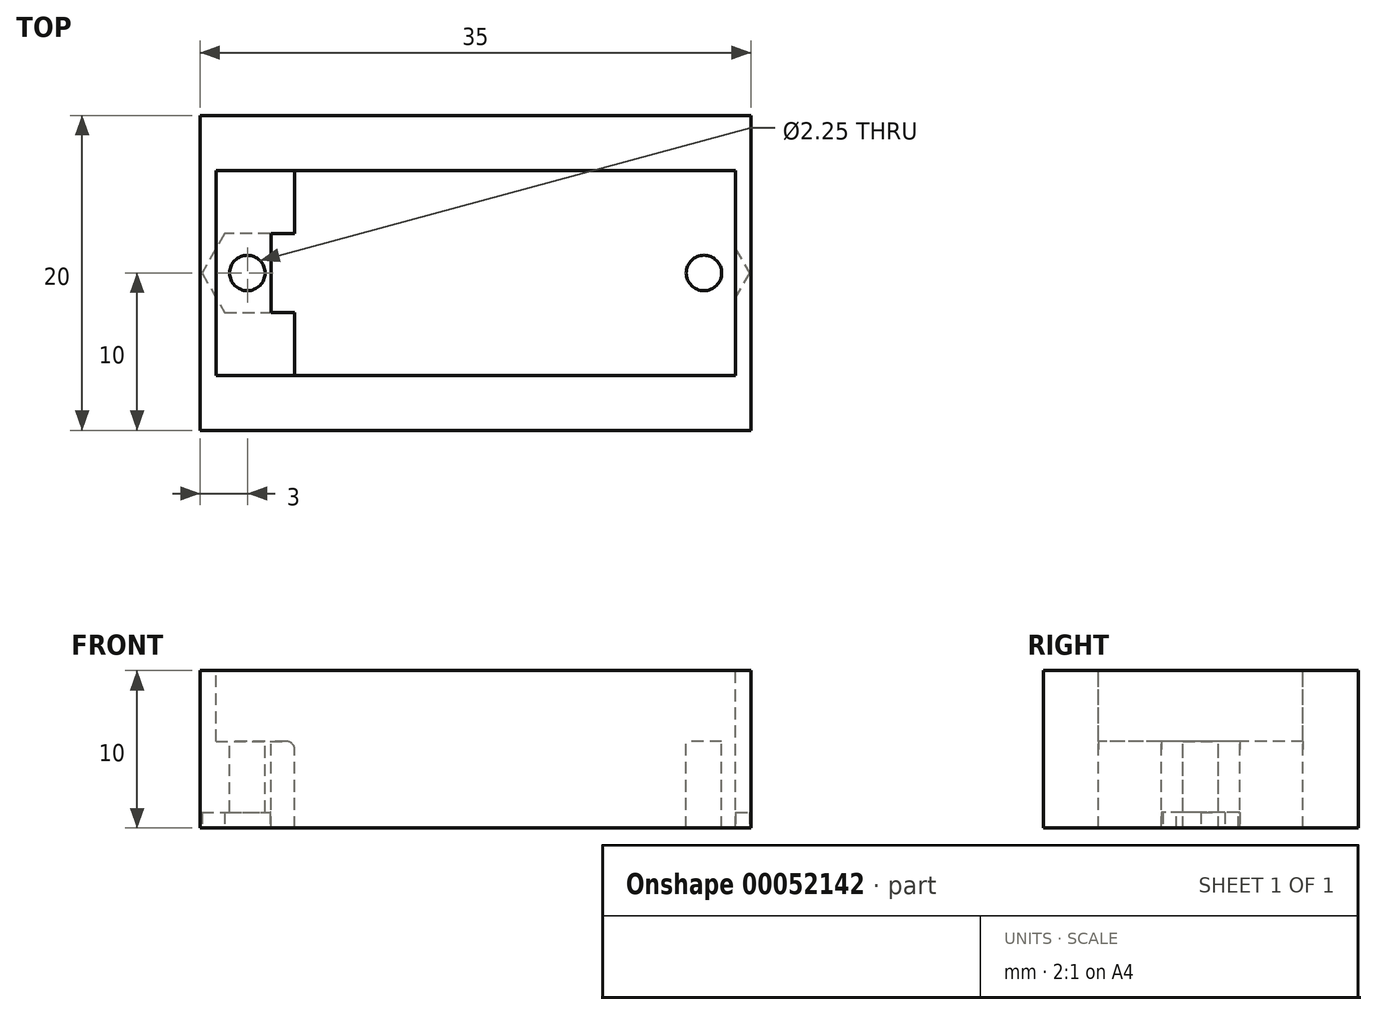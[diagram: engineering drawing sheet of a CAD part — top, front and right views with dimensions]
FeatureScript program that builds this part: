
annotation { "Feature Type Name" : "Feature", "Feature Type Description" : "" }
export const myFeature = defineFeature(function(context is Context, id is Id, definition is map)
    precondition{}
    {
        {
            var Q0;
            Q0=qCreatedBy(makeId("Top.planeOp"),FACE);
            var sketch = newSketch(context, id + "F0", { "sketchPlane" : qUnion([Q0])});
            skLineSegment(sketch, "E0.rect.bottom", {"start": v(-17.5, 10) * mm, "end": v(17.5, 10) * mm});
            skLineSegment(sketch, "E0.rect.top", {"start": v(-17.5, -10) * mm, "end": v(17.5, -10) * mm});
            skLineSegment(sketch, "E0.rect.left", {"start": v(-17.5, 10) * mm, "end": v(-17.5, -10) * mm});
            skLineSegment(sketch, "E0.rect.right", {"start": v(17.5, 10) * mm, "end": v(17.5, -10) * mm});
            skPoint(sketch, "E0.rect.middle", {"position": v(0, 0) * mm});
            skSolve(sketch);
        }
        {
            var Q0;
            Q0=makeQuery(id+"F0.imprint","IMPRINT",FACE,{"disambiguationData":[TD([[makeQuery(id+"F0.imprint","IMPRINT",EDGE,{"derivedFrom":sQuery(id+"F0.wireOp",EDGE,"E0.rect.bottom")}),-1.0]])]});
            extrude(context, id + "F1", {"entities" : qUnion([Q0]), "oppositeDirection" : true, "depth" : 10 * mm});
        }
        {
            var Q0;
            Q0=qCreatedBy(makeId("Top.planeOp"),FACE);
            var sketch = newSketch(context, id + "F2", { "sketchPlane" : qUnion([Q0])});
            skLineSegment(sketch, "E1.rect.bottom", {"start": v(11.5, -6.5) * mm, "end": v(-11.5, -6.5) * mm});
            skLineSegment(sketch, "E1.rect.top", {"start": v(11.5, 6.5) * mm, "end": v(-11.5, 6.5) * mm});
            skLineSegment(sketch, "E1.rect.left", {"start": v(11.5, -6.5) * mm, "end": v(11.5, 6.5) * mm});
            skLineSegment(sketch, "E1.rect.right", {"start": v(-11.5, -6.5) * mm, "end": v(-11.5, 6.5) * mm});
            skPoint(sketch, "E1.rect.middle", {"position": v(0, 0) * mm});
            skSolve(sketch);
        }
        {
            var Q0;
            Q0=makeQuery(id+"F2.imprint","IMPRINT",FACE,{"disambiguationData":[TD([[makeQuery(id+"F2.imprint","IMPRINT",EDGE,{"derivedFrom":sQuery(id+"F2.wireOp",EDGE,"E1.rect.bottom")}),-1.0]])]});
            var Q1;
            Q1=makeQuery(id+"F1.opExtrude","CAP_FACE",FACE,{"disambiguationData":[OSD([sQuery(id+"F0.wireOp",EDGE,"E0.rect.bottom"),sQuery(id+"F0.wireOp",EDGE,"E0.rect.top"),sQuery(id+"F0.wireOp",EDGE,"E0.rect.left"),sQuery(id+"F0.wireOp",EDGE,"E0.rect.right")])],"isStart":false});
            extrude(context, id + "F3", {"entities" : qUnion([Q0]), "operationType" : NewBodyOperationType.REMOVE, "endBound" : BoundingType.UP_TO_SURFACE, "oppositeDirection" : true, "endBoundEntityFace" : qUnion([Q1]), "depth" : 24 * mm});
        }
        {
            var Q0;
            Q0=qCreatedBy(makeId("Top.planeOp"),FACE);
            var sketch = newSketch(context, id + "F4", { "sketchPlane" : qUnion([Q0])});
            skLineSegment(sketch, "E2.rect.bottom", {"start": v(-16.5, 6.5) * mm, "end": v(16.5, 6.5) * mm});
            skLineSegment(sketch, "E2.rect.top", {"start": v(-16.5, -6.5) * mm, "end": v(16.5, -6.5) * mm});
            skLineSegment(sketch, "E2.rect.left", {"start": v(-16.5, 6.5) * mm, "end": v(-16.5, -6.5) * mm});
            skLineSegment(sketch, "E2.rect.right", {"start": v(16.5, 6.5) * mm, "end": v(16.5, -6.5) * mm});
            skPoint(sketch, "E2.rect.middle", {"position": v(0, 0) * mm});
            skSolve(sketch);
        }
        {
            var Q0;
            Q0=makeQuery(id+"F4.imprint","IMPRINT",FACE,{"disambiguationData":[TD([[makeQuery(id+"F4.imprint","IMPRINT",EDGE,{"derivedFrom":sQuery(id+"F4.wireOp",EDGE,"E2.rect.bottom")}),-1.0]])]});
            extrude(context, id + "F5", {"entities" : qUnion([Q0]), "operationType" : NewBodyOperationType.REMOVE, "oppositeDirection" : true, "depth" : 4.5 * mm});
        }
        {
            var Q0;
            Q0=makeQuery(id+"F5.boolean.opBoolean","COPY",FACE,{"disambiguationData":[OD(0.0)],"derivedFrom":makeQuery(id+"F5.opExtrude","CAP_FACE",FACE,{"disambiguationData":[OSD([sQuery(id+"F4.wireOp",EDGE,"E2.rect.bottom"),sQuery(id+"F4.wireOp",EDGE,"E2.rect.top"),sQuery(id+"F4.wireOp",EDGE,"E2.rect.left"),sQuery(id+"F4.wireOp",EDGE,"E2.rect.right")])],"isStart":false})});
            var sketch = newSketch(context, id + "F6", { "sketchPlane" : qUnion([Q0])});
            skCircle(sketch, "E3", {"center": v(-14.5, 0) * mm, "radius": 1.13 * mm});
            skPoint(sketch, "E3.centerSnap0", {"position": v(-11.5, 0) * mm});
            skCircle(sketch, "E4.MirrorC", {"center": v(14.5, 0) * mm, "radius": 1.13 * mm});
            skLineSegment(sketch, "E5.bottom", {"start": v(-11.5, 2.5) * mm, "end": v(-13, 2.5) * mm});
            skLineSegment(sketch, "E5.top", {"start": v(-11.5, -2.5) * mm, "end": v(-13, -2.5) * mm});
            skLineSegment(sketch, "E5.left", {"start": v(-11.5, 2.5) * mm, "end": v(-11.5, -2.5) * mm});
            skLineSegment(sketch, "E5.right", {"start": v(-13, 2.5) * mm, "end": v(-13, -2.5) * mm});
            skLineSegment(sketch, "E6.MirrorCS", {"start": v(11.5, 2.5) * mm, "end": v(13, 2.5) * mm});
            skLineSegment(sketch, "E7.MirrorCS", {"start": v(13, 2.5) * mm, "end": v(13, -2.5) * mm});
            skLineSegment(sketch, "E8.MirrorCS", {"start": v(11.5, -2.5) * mm, "end": v(13, -2.5) * mm});
            skLineSegment(sketch, "E9.MirrorCS", {"start": v(11.5, 2.5) * mm, "end": v(11.5, -2.5) * mm});
            skSolve(sketch);
        }
        {
            var Q0;
            Q0=makeQuery(id+"F6.imprint","IMPRINT",FACE,{"disambiguationData":[TD([[makeQuery(id+"F6.imprint","IMPRINT",EDGE,{"derivedFrom":sQuery(id+"F6.wireOp",EDGE,"E3")}),1.0]])]});
            var Q1;
            Q1=makeQuery(id+"F6.imprint","IMPRINT",FACE,{"disambiguationData":[TD([[makeQuery(id+"F6.imprint","IMPRINT",EDGE,{"derivedFrom":sQuery(id+"F6.wireOp",EDGE,"E4.MirrorC")}),-1.0]])]});
            var Q2;
            Q2=makeQuery(id+"F6.imprint","IMPRINT",FACE,{"disambiguationData":[TD([[makeQuery(id+"F6.imprint","IMPRINT",EDGE,{"derivedFrom":sQuery(id+"F6.wireOp",EDGE,"E5.bottom")}),1.0]])]});
            var Q3;
            Q3=makeQuery(id+"F6.imprint","IMPRINT",FACE,{"disambiguationData":[TD([[makeQuery(id+"F6.imprint","IMPRINT",EDGE,{"derivedFrom":sQuery(id+"F6.wireOp",EDGE,"E6.MirrorCS")}),-1.0]])]});
            var Q4;
            Q4=makeQuery(id+"F1.opExtrude","CAP_FACE",FACE,{"disambiguationData":[OSD([sQuery(id+"F0.wireOp",EDGE,"E0.rect.bottom"),sQuery(id+"F0.wireOp",EDGE,"E0.rect.top"),sQuery(id+"F0.wireOp",EDGE,"E0.rect.left"),sQuery(id+"F0.wireOp",EDGE,"E0.rect.right")])],"isStart":false});
            extrude(context, id + "F7", {"entities" : qUnion([Q0, Q1, Q2, Q3]), "operationType" : NewBodyOperationType.REMOVE, "endBound" : BoundingType.UP_TO_SURFACE, "oppositeDirection" : true, "endBoundEntityFace" : qUnion([Q4]), "depth" : 25 * mm});
        }
        {
            var Q0;
            Q0=makeQuery(id+"F1.opExtrude","CAP_FACE",FACE,{"disambiguationData":[OSD([sQuery(id+"F0.wireOp",EDGE,"E0.rect.bottom"),sQuery(id+"F0.wireOp",EDGE,"E0.rect.top"),sQuery(id+"F0.wireOp",EDGE,"E0.rect.left"),sQuery(id+"F0.wireOp",EDGE,"E0.rect.right")])],"isStart":false});
            var sketch = newSketch(context, id + "F8", { "sketchPlane" : qUnion([Q0])});
            skCircle(sketch, "E10.cCircle", {"center": v(-14.5, 0) * mm, "radius": 2.5 * mm, "construction": true});
            skLineSegment(sketch, "E10.0", {"start": v(-13.06, -2.5) * mm, "end": v(-15.94, -2.5) * mm});
            skLineSegment(sketch, "E10.1", {"start": v(-15.94, -2.5) * mm, "end": v(-17.39, 0) * mm});
            skLineSegment(sketch, "E10.2", {"start": v(-17.39, 0) * mm, "end": v(-15.94, 2.5) * mm});
            skLineSegment(sketch, "E10.3", {"start": v(-15.94, 2.5) * mm, "end": v(-13.06, 2.5) * mm});
            skLineSegment(sketch, "E10.4", {"start": v(-13.06, 2.5) * mm, "end": v(-11.61, 0) * mm});
            skLineSegment(sketch, "E10.5", {"start": v(-11.61, 0) * mm, "end": v(-13.06, -2.5) * mm});
            skPoint(sketch, "E10.0.midPoint", {"position": v(-14.5, -2.5) * mm});
            skCircle(sketch, "E11.MirrorC", {"center": v(14.5, 0) * mm, "radius": 2.5 * mm, "construction": true});
            skLineSegment(sketch, "E12.MirrorCS", {"start": v(15.94, -2.5) * mm, "end": v(17.39, 0) * mm});
            skLineSegment(sketch, "E13.MirrorCS", {"start": v(17.39, 0) * mm, "end": v(15.94, 2.5) * mm});
            skLineSegment(sketch, "E14.MirrorCS", {"start": v(15.94, 2.5) * mm, "end": v(13.06, 2.5) * mm});
            skLineSegment(sketch, "E15.MirrorCS", {"start": v(13.06, 2.5) * mm, "end": v(11.61, 0) * mm});
            skLineSegment(sketch, "E16.MirrorCS", {"start": v(11.61, 0) * mm, "end": v(13.06, -2.5) * mm});
            skLineSegment(sketch, "E17.MirrorCS", {"start": v(13.06, -2.5) * mm, "end": v(15.94, -2.5) * mm});
            skSolve(sketch);
        }
        {
            var Q0;
            {var subQ1=sQuery(id+"F8.wireOp",EDGE,"E10.0");Q0=makeQuery(id+"F8.imprint","IMPRINT",FACE,{"disambiguationData":[TD([[makeQuery(id+"F8.imprint","IMPRINT",EDGE,{"derivedFrom":subQ1}),-1.0]])]});}
            var Q1;
            Q1=makeQuery(id+"F8.imprint","IMPRINT",FACE,{"disambiguationData":[TD([[makeQuery(id+"F8.imprint","IMPRINT",EDGE,{"derivedFrom":sQuery(id+"F8.wireOp",EDGE,"E12.MirrorCS")}),1.0]])]});
            extrude(context, id + "F9", {"entities" : qUnion([Q0, Q1]), "operationType" : NewBodyOperationType.REMOVE, "oppositeDirection" : true, "depth" : 1 * mm});
        }
        {
            var Q0;
            {var subQ0=sQuery(id+"F2.wireOp",EDGE,"E1.rect.right");Q0=makeQuery(id+"F7.boolean.opBoolean","SPLIT",EDGE,{"disambiguationData":[TD([makeQuery(id+"F3.boolean.opBoolean","COPY",FACE,{"derivedFrom":makeQuery(id+"F3.opExtrude","SWEPT_FACE",FACE,{"disambiguationData":[OSD([sQuery(id+"F2.wireOp",EDGE,"E1.rect.top")])]})})])],"derivedFrom":makeQuery(id+"F3.boolean.opBoolean","COPY",EDGE,{"derivedFrom":makeQuery(id+"F3.opExtrude","CAP_EDGE",EDGE,{"disambiguationData":[OSD([subQ0])],"isStart":false})})});}
            var Q1;
            {var subQ0=sQuery(id+"F2.wireOp",EDGE,"E1.rect.right");Q1=makeQuery(id+"F7.boolean.opBoolean","SPLIT",EDGE,{"disambiguationData":[TD([makeQuery(id+"F3.boolean.opBoolean","COPY",FACE,{"derivedFrom":makeQuery(id+"F3.opExtrude","SWEPT_FACE",FACE,{"disambiguationData":[OSD([sQuery(id+"F2.wireOp",EDGE,"E1.rect.bottom")])]})})])],"derivedFrom":makeQuery(id+"F3.boolean.opBoolean","COPY",EDGE,{"derivedFrom":makeQuery(id+"F3.opExtrude","CAP_EDGE",EDGE,{"disambiguationData":[OSD([subQ0])],"isStart":false})})});}
            var Q2;
            Q2=makeQuery(id+"F3.boolean.opBoolean","COPY",EDGE,{"derivedFrom":makeQuery(id+"F3.opExtrude","CAP_EDGE",EDGE,{"disambiguationData":[OSD([sQuery(id+"F2.wireOp",EDGE,"E1.rect.bottom")])],"isStart":false})});
            var Q3;
            Q3=makeQuery(id+"F3.boolean.opBoolean","COPY",EDGE,{"derivedFrom":makeQuery(id+"F3.opExtrude","CAP_EDGE",EDGE,{"disambiguationData":[OSD([sQuery(id+"F2.wireOp",EDGE,"E1.rect.top")])],"isStart":false})});
            var Q4;
            {var subQ0=sQuery(id+"F2.wireOp",EDGE,"E1.rect.left");Q4=makeQuery(id+"F7.boolean.opBoolean","SPLIT",EDGE,{"disambiguationData":[TD([makeQuery(id+"F3.boolean.opBoolean","COPY",FACE,{"derivedFrom":makeQuery(id+"F3.opExtrude","SWEPT_FACE",FACE,{"disambiguationData":[OSD([sQuery(id+"F2.wireOp",EDGE,"E1.rect.top")])]})})])],"derivedFrom":makeQuery(id+"F3.boolean.opBoolean","COPY",EDGE,{"derivedFrom":makeQuery(id+"F3.opExtrude","CAP_EDGE",EDGE,{"disambiguationData":[OSD([subQ0])],"isStart":false})})});}
            var Q5;
            {var subQ0=sQuery(id+"F2.wireOp",EDGE,"E1.rect.left");Q5=makeQuery(id+"F7.boolean.opBoolean","SPLIT",EDGE,{"disambiguationData":[TD([makeQuery(id+"F3.boolean.opBoolean","COPY",FACE,{"derivedFrom":makeQuery(id+"F3.opExtrude","SWEPT_FACE",FACE,{"disambiguationData":[OSD([sQuery(id+"F2.wireOp",EDGE,"E1.rect.bottom")])]})})])],"derivedFrom":makeQuery(id+"F3.boolean.opBoolean","COPY",EDGE,{"derivedFrom":makeQuery(id+"F3.opExtrude","CAP_EDGE",EDGE,{"disambiguationData":[OSD([subQ0])],"isStart":false})})});}
            var Q6;
            {var subQ0=sQuery(id+"F4.wireOp",EDGE,"E2.rect.top");var subQ1=makeQuery(id+"F5.opExtrude","CAP_FACE",FACE,{"disambiguationData":[OSD([sQuery(id+"F4.wireOp",EDGE,"E2.rect.bottom"),subQ0,sQuery(id+"F4.wireOp",EDGE,"E2.rect.left"),sQuery(id+"F4.wireOp",EDGE,"E2.rect.right")])],"isStart":false});var subQ2=makeQuery(id+"F3.boolean.opBoolean","COPY",FACE,{"derivedFrom":makeQuery(id+"F3.opExtrude","SWEPT_FACE",FACE,{"disambiguationData":[OSD([sQuery(id+"F2.wireOp",EDGE,"E1.rect.left")])]})});Q6=makeQuery(id+"F7.boolean.opBoolean","SPLIT",EDGE,{"disambiguationData":[TD([makeQuery(id+"F3.boolean.opBoolean","COPY",FACE,{"derivedFrom":makeQuery(id+"F3.opExtrude","SWEPT_FACE",FACE,{"disambiguationData":[OSD([sQuery(id+"F2.wireOp",EDGE,"E1.rect.bottom")])]})})])],"derivedFrom":makeQuery(id+"F5.boolean.opBoolean","INTERSECT",EDGE,{"derivedFrom":[subQ2,subQ1]})});}
            var Q7;
            {var subQ0=sQuery(id+"F4.wireOp",EDGE,"E2.rect.bottom");var subQ1=makeQuery(id+"F5.opExtrude","CAP_FACE",FACE,{"disambiguationData":[OSD([subQ0,sQuery(id+"F4.wireOp",EDGE,"E2.rect.top"),sQuery(id+"F4.wireOp",EDGE,"E2.rect.left"),sQuery(id+"F4.wireOp",EDGE,"E2.rect.right")])],"isStart":false});var subQ2=makeQuery(id+"F3.boolean.opBoolean","COPY",FACE,{"derivedFrom":makeQuery(id+"F3.opExtrude","SWEPT_FACE",FACE,{"disambiguationData":[OSD([sQuery(id+"F2.wireOp",EDGE,"E1.rect.left")])]})});Q7=makeQuery(id+"F7.boolean.opBoolean","SPLIT",EDGE,{"disambiguationData":[TD([makeQuery(id+"F3.boolean.opBoolean","COPY",FACE,{"derivedFrom":makeQuery(id+"F3.opExtrude","SWEPT_FACE",FACE,{"disambiguationData":[OSD([sQuery(id+"F2.wireOp",EDGE,"E1.rect.top")])]})})])],"derivedFrom":makeQuery(id+"F5.boolean.opBoolean","INTERSECT",EDGE,{"derivedFrom":[subQ2,subQ1]})});}
            var Q8;
            {var subQ0=sQuery(id+"F4.wireOp",EDGE,"E2.rect.top");var subQ1=makeQuery(id+"F5.opExtrude","CAP_FACE",FACE,{"disambiguationData":[OSD([sQuery(id+"F4.wireOp",EDGE,"E2.rect.bottom"),subQ0,sQuery(id+"F4.wireOp",EDGE,"E2.rect.left"),sQuery(id+"F4.wireOp",EDGE,"E2.rect.right")])],"isStart":false});var subQ2=makeQuery(id+"F3.boolean.opBoolean","COPY",FACE,{"derivedFrom":makeQuery(id+"F3.opExtrude","SWEPT_FACE",FACE,{"disambiguationData":[OSD([sQuery(id+"F2.wireOp",EDGE,"E1.rect.right")])]})});Q8=makeQuery(id+"F7.boolean.opBoolean","SPLIT",EDGE,{"disambiguationData":[TD([makeQuery(id+"F3.boolean.opBoolean","COPY",FACE,{"derivedFrom":makeQuery(id+"F3.opExtrude","SWEPT_FACE",FACE,{"disambiguationData":[OSD([sQuery(id+"F2.wireOp",EDGE,"E1.rect.bottom")])]})})])],"derivedFrom":makeQuery(id+"F5.boolean.opBoolean","INTERSECT",EDGE,{"derivedFrom":[subQ2,subQ1]})});}
            var Q9;
            {var subQ0=sQuery(id+"F4.wireOp",EDGE,"E2.rect.bottom");var subQ1=makeQuery(id+"F5.opExtrude","CAP_FACE",FACE,{"disambiguationData":[OSD([subQ0,sQuery(id+"F4.wireOp",EDGE,"E2.rect.top"),sQuery(id+"F4.wireOp",EDGE,"E2.rect.left"),sQuery(id+"F4.wireOp",EDGE,"E2.rect.right")])],"isStart":false});var subQ2=makeQuery(id+"F3.boolean.opBoolean","COPY",FACE,{"derivedFrom":makeQuery(id+"F3.opExtrude","SWEPT_FACE",FACE,{"disambiguationData":[OSD([sQuery(id+"F2.wireOp",EDGE,"E1.rect.right")])]})});Q9=makeQuery(id+"F7.boolean.opBoolean","SPLIT",EDGE,{"disambiguationData":[TD([makeQuery(id+"F3.boolean.opBoolean","COPY",FACE,{"derivedFrom":makeQuery(id+"F3.opExtrude","SWEPT_FACE",FACE,{"disambiguationData":[OSD([sQuery(id+"F2.wireOp",EDGE,"E1.rect.top")])]})})])],"derivedFrom":makeQuery(id+"F5.boolean.opBoolean","INTERSECT",EDGE,{"derivedFrom":[subQ2,subQ1]})});}
            fillet(context, id + "F10", {"entities" : qUnion([Q0, Q1, Q2, Q3, Q4, Q5, Q6, Q7, Q8, Q9]), "radius" : 0.5 * mm, "tangentPropagation" : true, "allowEdgeOverflow" : false});
        }
    });
